# Revit family: BIMLIB_ПланкаПримыканиеВерхнееКТрубеФальц_GRANDLINE
name_source: partatom
category: Обобщенные модели
revit_build: Autodesk Revit 2017 (Build: 20170118_1100(x64)
units: mm (PartAtom-declared; Revit-internal decimal feet)

## family parameters
Может служить основой для арматурных стержней = Нет
Общий = Нет
При загрузке вырезать с полостями = Нет
Размер круглого соединителя = Использовать диаметр
Тип детали = Нормальный
Точка расчета площади = Нет

## types (1)
- Планка примыкание верхнее к трубе фальц
    ADSK_Версия Revit = 2017
    ADSK_Группирование = Доборные элементы
    ADSK_Единица измерения = м
    ADSK_Завод-изготовитель = Grand Line
    ADSK_Код изделия = М.15.025.006
    ADSK_Материал = GL_Сталь_RAL9005
    ADSK_Материал тип подсчета = 1
    ADSK_Наименование = Планка примыкание верхнее к трубе фальц
    ADSK_Обозначение = ГОСТ 19904-90, ГОСТ 14918-80
    BL_BIM library = https://bimlib.pro
    URL = https://www.grandline.ru
    Изготовитель = Grand Line
    Описание = Планка примыкание верхнее к трубе фальц
    Смещение = 0 мм
